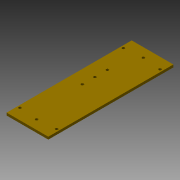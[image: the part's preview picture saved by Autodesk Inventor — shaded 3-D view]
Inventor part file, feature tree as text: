
AUTODESK INVENTOR PART (.ipt)
format: ipt  version: 2013 SP2 (Build 170200200, 200)  size: 91,648 bytes
history: native  units: mm
features: reference x8, extrude x2, sketch x1
ambient origin geometry x8: Origin, YZ Plane, XZ Plane, XY Plane, X Axis, Y Axis, Z Axis, Center Point
bodies: Solid1 (feature_tree)
feature tree (11):
  extrude  "Extrusion1"  Depth=3.0mm
  extrude  "Extrusion3"  Depth=150.0mm TaperAngle=0.0deg
  sketch  "Sketch1"  dims[d0=50.0mm d1=3.0mm d2=150.0mm d3=0.0mm d16=10.0mm d17=0.0mm d18=3.2mm d19=3.2mm d20=15.0mm d21=15.0mm]
  reference  "Reference29"
  reference  "Reference30"
  reference  "Reference31"
  reference  "Reference32"
  reference  "Reference33"
  reference  "Reference34"
  reference  "Reference35"
  reference  "Reference37"
